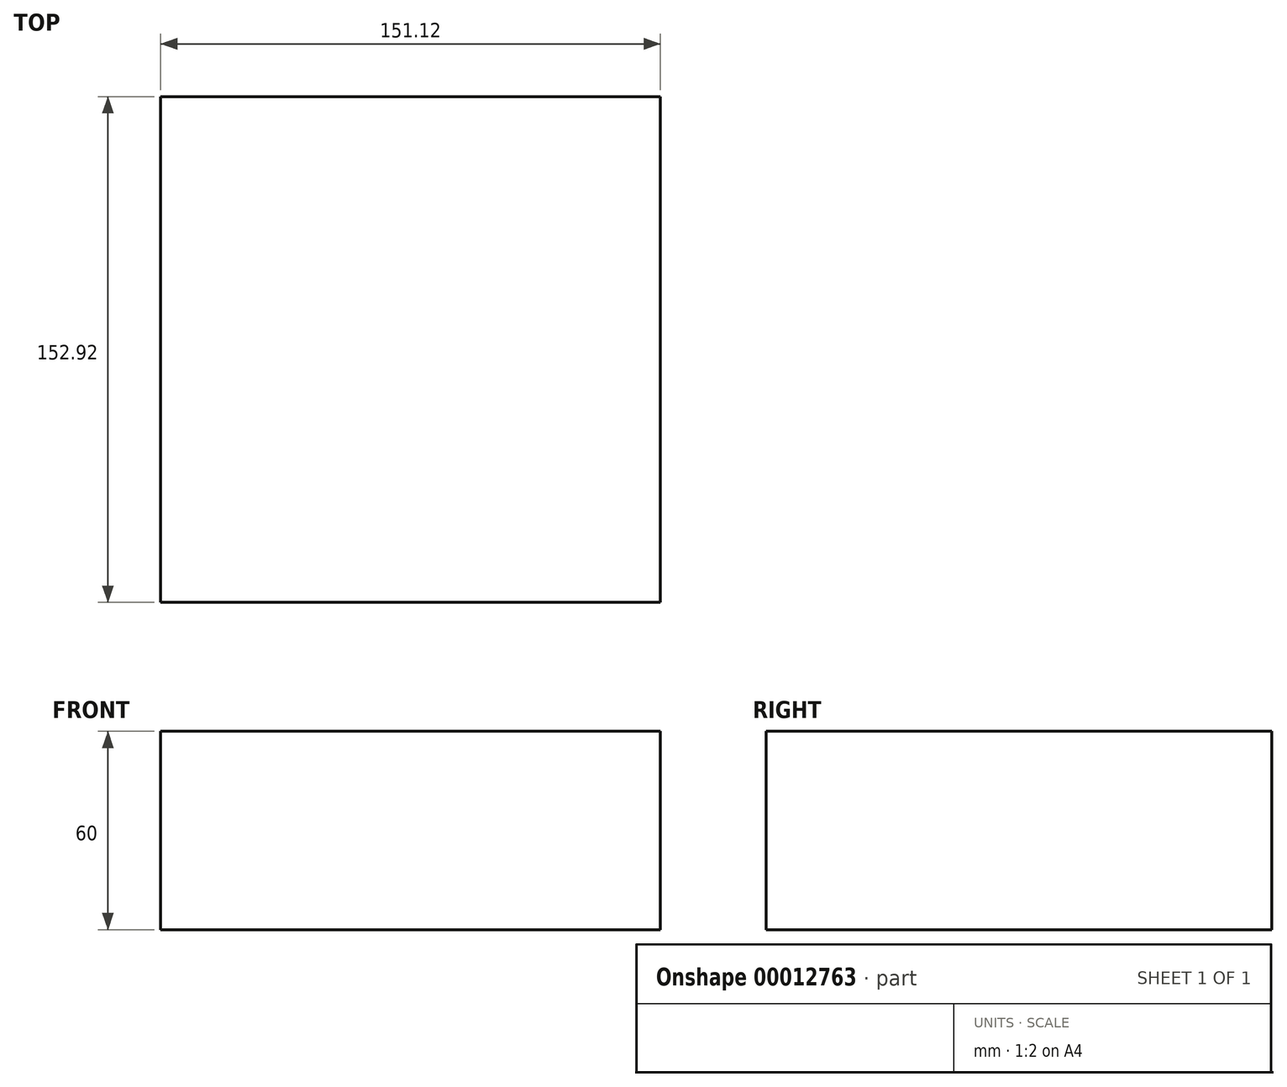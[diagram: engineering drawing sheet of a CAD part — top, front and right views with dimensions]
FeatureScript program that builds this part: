
annotation { "Feature Type Name" : "Feature", "Feature Type Description" : "" }
export const myFeature = defineFeature(function(context is Context, id is Id, definition is map)
    precondition{}
    {
        {
            var Q0;
            Q0=qCreatedBy(makeId("Top.planeOp"),FACE);
            var sketch = newSketch(context, id + "F0", { "sketchPlane" : qUnion([Q0])});
            skLineSegment(sketch, "E0.bottom", {"start": v(74.5, 71.88) * mm, "end": v(-76.62, 71.88) * mm});
            skLineSegment(sketch, "E0.top", {"start": v(74.5, -81.04) * mm, "end": v(-76.62, -81.04) * mm});
            skLineSegment(sketch, "E0.left", {"start": v(74.5, 71.88) * mm, "end": v(74.5, -81.04) * mm});
            skLineSegment(sketch, "E0.right", {"start": v(-76.62, 71.88) * mm, "end": v(-76.62, -81.04) * mm});
            skSolve(sketch);
        }
        {
            var Q0;
            Q0=makeQuery(id+"F0.imprint","IMPRINT",FACE,{"disambiguationData":[TD([[makeQuery(id+"F0.imprint","IMPRINT",EDGE,{"derivedFrom":sQuery(id+"F0.wireOp",EDGE,"E0.bottom")}),1.0]])]});
            extrude(context, id + "F1", {"entities" : qUnion([Q0]), "depth" : 60 * mm});
        }
    });
